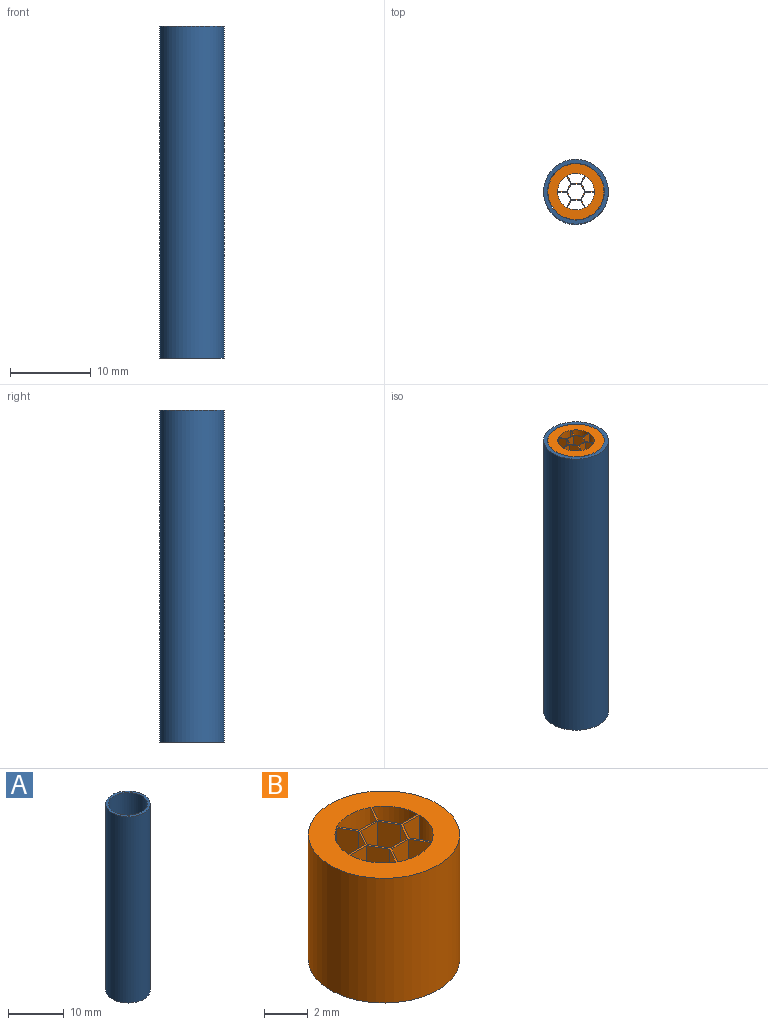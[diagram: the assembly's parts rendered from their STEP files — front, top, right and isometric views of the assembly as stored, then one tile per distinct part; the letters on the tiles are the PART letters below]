
ASSEMBLY  parts=2 mates=1
PART A: 4 faces, bbox 8x8x41 mm
  f0: cylinder r=4mm len=41mm, axis (0,0,-1), area 1030.4mm2, adj f1,f2
  f1: plane 8x8mm, normal (0,0,1), area 11.8mm2, adj f0,f3
  f2: plane 8x8mm, normal (0,0,-1), area 11.8mm2, adj f0,f3
  f3: cylinder r=3.5mm len=41mm, axis (0,0,1), area 901.6mm2, adj f1,f2
PART B: 33 faces, bbox 6.9x6.9x7 mm
  f0: plane 6.94x6.94mm, normal (0,0,1), area 23.2mm2, adj f2,f3,f4,f5,f6,f7,f8,f9
  f1: plane 6.94x6.94mm, normal (0,0,-1), area 23.2mm2, adj f2,f3,f4,f5,f6,f7,f8,f9
  f2: cylinder r=3.47mm len=7mm, axis (0,0,-1), area 152.6mm2, adj f0,f1
  f3: plane 7x0.92mm, normal (-0.87,-0.5,0), area 7.5mm2, adj f0,f1,f4,f6
  f4: cylinder r=2.25mm len=7mm, axis (0,0,1), area 15.8mm2, adj f0,f1,f3,f5
  f5: plane 7x1.07mm, normal (0,1,0), area 7.5mm2, adj f0,f1,f4,f6
  f6: plane 7x0.95mm, normal (-0.87,0.5,0), area 7.7mm2, adj f0,f1,f3,f5
  f7: plane 7x0.92mm, normal (-0.87,-0.5,0), area 7.5mm2, adj f0,f1,f8,f10
  f8: plane 7x1.1mm, normal (0,-1,0), area 7.7mm2, adj f0,f1,f7,f9
  f9: plane 7x0.92mm, normal (0.87,-0.5,0), area 7.5mm2, adj f0,f1,f8,f10
  f10: cylinder r=2.25mm len=7mm, axis (0,0,1), area 15.8mm2, adj f0,f1,f7,f9
  f11: plane 7x1.07mm, normal (0,-1,0), area 7.5mm2, adj f0,f1,f12,f14
  f12: cylinder r=2.25mm len=7mm, axis (0,0,1), area 15.8mm2, adj f0,f1,f11,f13
  f13: plane 7x0.92mm, normal (-0.87,0.5,0), area 7.5mm2, adj f0,f1,f12,f14
  f14: plane 7x0.95mm, normal (-0.87,-0.5,0), area 7.7mm2, adj f0,f1,f11,f13
  f15: plane 7x0.92mm, normal (0.87,-0.5,0), area 7.5mm2, adj f0,f1,f16,f18
  f16: plane 7x0.95mm, normal (0.87,0.5,0), area 7.7mm2, adj f0,f1,f15,f17
  f17: plane 7x1.07mm, normal (0,1,0), area 7.5mm2, adj f0,f1,f16,f18
  f18: cylinder r=2.25mm len=7mm, axis (0,0,1), area 15.8mm2, adj f0,f1,f15,f17
  f19: plane 7x0.92mm, normal (-0.87,0.5,0), area 7.5mm2, adj f0,f1,f20,f22
  f20: cylinder r=2.25mm len=7mm, axis (0,0,1), area 15.8mm2, adj f0,f1,f19,f21
  f21: plane 7x0.92mm, normal (0.87,0.5,0), area 7.5mm2, adj f0,f1,f20,f22
  f22: plane 7x1.1mm, normal (0,1,0), area 7.7mm2, adj f0,f1,f19,f21
  f23: plane 7x1.07mm, normal (0,-1,0), area 7.5mm2, adj f0,f1,f24,f26
  f24: plane 7x0.95mm, normal (0.87,-0.5,0), area 7.7mm2, adj f0,f1,f23,f25
  f25: plane 7x0.92mm, normal (0.87,0.5,0), area 7.5mm2, adj f0,f1,f24,f26
  f26: cylinder r=2.25mm len=7mm, axis (0,0,1), area 15.8mm2, adj f0,f1,f23,f25
  f27: plane 7x0.95mm, normal (-0.87,0.5,0), area 7.7mm2, adj f0,f1,f28,f32
  f28: plane 7x0.95mm, normal (-0.87,-0.5,0), area 7.7mm2, adj f0,f1,f27,f29
  f29: plane 7x1.1mm, normal (0,-1,0), area 7.7mm2, adj f0,f1,f28,f30
  f30: plane 7x0.95mm, normal (0.87,-0.5,0), area 7.7mm2, adj f0,f1,f29,f31
  f31: plane 7x0.95mm, normal (0.87,0.5,0), area 7.7mm2, adj f0,f1,f30,f32
  f32: plane 7x1.1mm, normal (0,1,0), area 7.7mm2, adj f0,f1,f27,f31
PLACE A t=(-0.01,-0.02,-71.52)mm
PLACE B t=(-0.01,-0.02,-37.52)mm
MATE planar A.f0 <-> B.f2  axis (0,0,1) through (-0.01,-0.02,-30.52)mm
